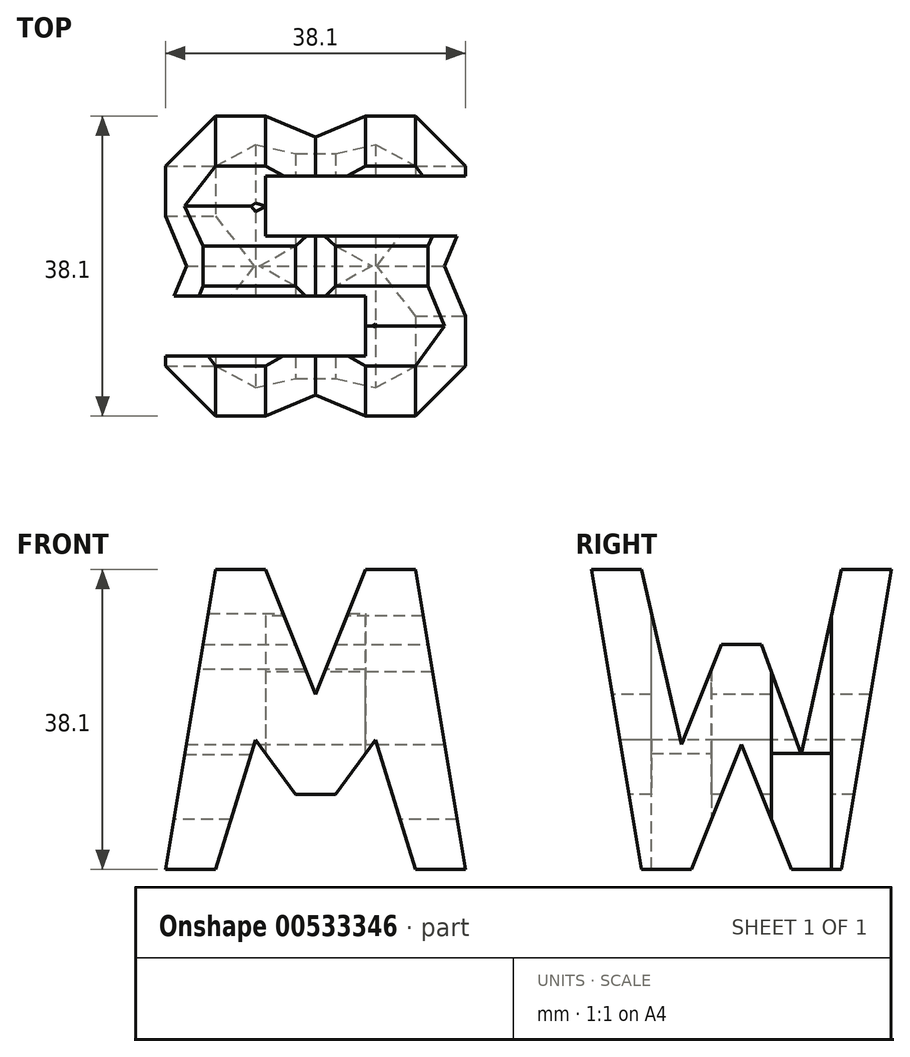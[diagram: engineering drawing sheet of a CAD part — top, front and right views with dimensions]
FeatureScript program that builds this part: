
annotation { "Feature Type Name" : "Feature", "Feature Type Description" : "" }
export const myFeature = defineFeature(function(context is Context, id is Id, definition is map)
    precondition{}
    {
        {
            var Q0;
            Q0=qCreatedBy(makeId("Front.planeOp"),FACE);
            var sketch = newSketch(context, id + "F0", { "sketchPlane" : qUnion([Q0])});
            skLineSegment(sketch, "E0", {"start": v(0, 0) * mm, "end": v(0, 38.1) * mm});
            skLineSegment(sketch, "E1", {"start": v(0, 38.1) * mm, "end": v(38.1, 38.1) * mm});
            skLineSegment(sketch, "E2", {"start": v(38.1, 38.1) * mm, "end": v(38.1, 0) * mm});
            skLineSegment(sketch, "E3", {"start": v(38.1, 0) * mm, "end": v(0, 0) * mm});
            skSolve(sketch);
        }
        {
            var Q0;
            Q0 = qSketchRegion(id + "F0", true);
            extrude(context, id + "F1", {"entities" : qUnion([Q0]), "depth" : 38.1 * mm, "offsetDistance" : 25.4 * mm});
        }
        {
            var Q0;
            Q0=qCreatedBy(makeId("Front.planeOp"),FACE);
            cPlane(context, id + "F2", {"entities" : qUnion([Q0]), "cplaneType" : CPlaneType.OFFSET, "offset" : 38.1 * mm, "width" : 152.4 * mm, "height" : 152.4 * mm});
        }
        {
            var Q0;
            Q0=qCreatedBy(makeId("Right.planeOp"),FACE);
            cPlane(context, id + "F3", {"entities" : qUnion([Q0]), "cplaneType" : CPlaneType.OFFSET, "offset" : 38.1 * mm, "width" : 152.4 * mm, "height" : 152.4 * mm});
        }
        {
            var Q0;
            Q0=qCreatedBy(makeId("Top.planeOp"),FACE);
            cPlane(context, id + "F4", {"entities" : qUnion([Q0]), "cplaneType" : CPlaneType.OFFSET, "offset" : 38.1 * mm, "width" : 152.4 * mm, "height" : 152.4 * mm});
        }
        {
            var Q0;
            Q0=qCreatedBy(id+"F3.planeOp",FACE);
            var sketch = newSketch(context, id + "F5", { "sketchPlane" : qUnion([Q0])});
            skLineSegment(sketch, "E4", {"start": v(0, 0) * mm, "end": v(0, 38.1) * mm});
            skLineSegment(sketch, "E5", {"start": v(0, 38.1) * mm, "end": v(-38.1, 38.1) * mm});
            skLineSegment(sketch, "E6", {"start": v(-38.1, 38.1) * mm, "end": v(-38.1, 0) * mm});
            skLineSegment(sketch, "E7", {"start": v(-38.1, 0) * mm, "end": v(0, 0) * mm});
            skLineSegment(sketch, "E8", {"start": v(-31.75, 38.1) * mm, "end": v(-26.67, 15.88) * mm});
            skLineSegment(sketch, "E9", {"start": v(-26.67, 15.88) * mm, "end": v(-21.59, 28.58) * mm});
            skLineSegment(sketch, "E10", {"start": v(-21.59, 28.58) * mm, "end": v(-16.5, 28.58) * mm});
            skPoint(sketch, "E11.start.orphan", {"position": v(-19.05, 15.88) * mm});
            skPoint(sketch, "E12.end.orphan", {"position": v(-4.03, 38.1) * mm});
            skLineSegment(sketch, "E13", {"start": v(-38.1, 38.1) * mm, "end": v(-31.75, 0) * mm});
            skLineSegment(sketch, "E14", {"start": v(-25.4, 0) * mm, "end": v(-19.05, 15.88) * mm});
            skLineSegment(sketch, "E15", {"start": v(-19.05, 15.88) * mm, "end": v(-12.7, 0) * mm});
            skLineSegment(sketch, "E16", {"start": v(0, 38.1) * mm, "end": v(-6.35, 0) * mm});
            skPoint(sketch, "E17.end.orphan", {"position": v(-6.35, 38.1) * mm});
            skLineSegment(sketch, "E18", {"start": v(-6.35, 38.1) * mm, "end": v(-11.43, 14.59) * mm});
            skPoint(sketch, "E19.end.orphan", {"position": v(-16.7, 15.88) * mm});
            skLineSegment(sketch, "E20", {"start": v(-16.5, 28.58) * mm, "end": v(-11.43, 14.59) * mm});
            skSolve(sketch);
        }
        {
            var Q0;
            {var subQ0=sQuery(id+"F5.wireOp",EDGE,"E8");Q0=makeQuery(id+"F5.imprint","IMPRINT",FACE,{"disambiguationData":[TD([[makeQuery(id+"F5.imprint","IMPRINT",EDGE,{"derivedFrom":subQ0}),1.0]])]});}
            var Q1;
            {var subQ0=sQuery(id+"F5.wireOp",EDGE,"E6");Q1=makeQuery(id+"F5.imprint","IMPRINT",FACE,{"disambiguationData":[TD([[makeQuery(id+"F5.imprint","IMPRINT",EDGE,{"derivedFrom":subQ0}),1.0]])]});}
            var Q2;
            {var subQ0=sQuery(id+"F5.wireOp",EDGE,"E14");Q2=makeQuery(id+"F5.imprint","IMPRINT",FACE,{"disambiguationData":[TD([[makeQuery(id+"F5.imprint","IMPRINT",EDGE,{"derivedFrom":subQ0}),-1.0]])]});}
            var Q3;
            {var subQ0=sQuery(id+"F5.wireOp",EDGE,"E4");Q3=makeQuery(id+"F5.imprint","IMPRINT",FACE,{"disambiguationData":[TD([[makeQuery(id+"F5.imprint","IMPRINT",EDGE,{"derivedFrom":subQ0}),1.0]])]});}
            extrude(context, id + "F6", {"entities" : qUnion([Q0, Q1, Q2, Q3]), "operationType" : NewBodyOperationType.REMOVE, "oppositeDirection" : true, "depth" : 38.1 * mm, "offsetDistance" : 25.4 * mm});
        }
        {
            var Q0;
            Q0=qCreatedBy(id+"F2.planeOp",FACE);
            var sketch = newSketch(context, id + "F7", { "sketchPlane" : qUnion([Q0])});
            skLineSegment(sketch, "E21", {"start": v(0, 0) * mm, "end": v(0, 38.1) * mm});
            skLineSegment(sketch, "E22", {"start": v(0, 38.1) * mm, "end": v(38.1, 38.1) * mm});
            skLineSegment(sketch, "E23", {"start": v(38.1, 38.1) * mm, "end": v(38.1, 0) * mm});
            skLineSegment(sketch, "E24", {"start": v(38.1, 0) * mm, "end": v(0, 0) * mm});
            skLineSegment(sketch, "E25", {"start": v(0, 0) * mm, "end": v(6.35, 38.1) * mm});
            skLineSegment(sketch, "E26", {"start": v(12.7, 38.1) * mm, "end": v(19.05, 22.22) * mm});
            skLineSegment(sketch, "E27", {"start": v(19.05, 22.22) * mm, "end": v(25.4, 38.1) * mm});
            skLineSegment(sketch, "E28", {"start": v(38.1, 0) * mm, "end": v(31.75, 38.1) * mm});
            skLineSegment(sketch, "E29", {"start": v(6.35, 0) * mm, "end": v(11.43, 16.47) * mm});
            skLineSegment(sketch, "E30", {"start": v(11.43, 16.47) * mm, "end": v(16.51, 9.52) * mm});
            skLineSegment(sketch, "E31", {"start": v(16.51, 9.52) * mm, "end": v(21.6, 9.52) * mm});
            skLineSegment(sketch, "E32", {"start": v(21.6, 9.52) * mm, "end": v(26.67, 16.47) * mm});
            skLineSegment(sketch, "E33", {"start": v(26.67, 16.47) * mm, "end": v(31.75, 0) * mm});
            skSolve(sketch);
        }
        {
            var Q0;
            {var subQ0=sQuery(id+"F7.wireOp",EDGE,"E21");Q0=makeQuery(id+"F7.imprint","IMPRINT",FACE,{"disambiguationData":[TD([[makeQuery(id+"F7.imprint","IMPRINT",EDGE,{"derivedFrom":subQ0}),-1.0]])]});}
            var Q1;
            {var subQ0=sQuery(id+"F7.wireOp",EDGE,"E26");Q1=makeQuery(id+"F7.imprint","IMPRINT",FACE,{"disambiguationData":[TD([[makeQuery(id+"F7.imprint","IMPRINT",EDGE,{"derivedFrom":subQ0}),1.0]])]});}
            var Q2;
            {var subQ0=sQuery(id+"F7.wireOp",EDGE,"E29");Q2=makeQuery(id+"F7.imprint","IMPRINT",FACE,{"disambiguationData":[TD([[makeQuery(id+"F7.imprint","IMPRINT",EDGE,{"derivedFrom":subQ0}),-1.0]])]});}
            var Q3;
            {var subQ0=sQuery(id+"F7.wireOp",EDGE,"E23");Q3=makeQuery(id+"F7.imprint","IMPRINT",FACE,{"disambiguationData":[TD([[makeQuery(id+"F7.imprint","IMPRINT",EDGE,{"derivedFrom":subQ0}),-1.0]])]});}
            extrude(context, id + "F8", {"entities" : qUnion([Q0, Q1, Q2, Q3]), "operationType" : NewBodyOperationType.REMOVE, "oppositeDirection" : true, "depth" : 38.1 * mm, "offsetDistance" : 25.4 * mm});
        }
        {
            var Q0;
            Q0=qCreatedBy(id+"F4.planeOp",FACE);
            var sketch = newSketch(context, id + "F9", { "sketchPlane" : qUnion([Q0])});
            skLineSegment(sketch, "E34", {"start": v(0, 0) * mm, "end": v(38.1, 0) * mm});
            skLineSegment(sketch, "E35", {"start": v(38.1, 0) * mm, "end": v(38.1, -38.1) * mm});
            skLineSegment(sketch, "E36", {"start": v(38.1, -38.1) * mm, "end": v(0, -38.1) * mm});
            skLineSegment(sketch, "E37", {"start": v(0, 0) * mm, "end": v(0, -38.1) * mm});
            skLineSegment(sketch, "E38", {"start": v(0, -22.86) * mm, "end": v(25.4, -22.86) * mm});
            skLineSegment(sketch, "E39", {"start": v(25.4, -22.86) * mm, "end": v(25.4, -30.48) * mm});
            skLineSegment(sketch, "E40", {"start": v(25.4, -30.48) * mm, "end": v(0, -30.48) * mm});
            skLineSegment(sketch, "E41", {"start": v(38.1, -7.62) * mm, "end": v(12.7, -7.62) * mm});
            skLineSegment(sketch, "E42", {"start": v(12.7, -7.62) * mm, "end": v(12.7, -15.24) * mm});
            skLineSegment(sketch, "E43", {"start": v(12.7, -15.24) * mm, "end": v(38.1, -15.24) * mm});
            skSolve(sketch);
        }
        {
            var Q0;
            {var subQ0=sQuery(id+"F9.wireOp",EDGE,"E41");Q0=makeQuery(id+"F9.imprint","IMPRINT",FACE,{"disambiguationData":[TD([[makeQuery(id+"F9.imprint","IMPRINT",EDGE,{"derivedFrom":subQ0}),1.0]])]});}
            var Q1;
            {var subQ0=sQuery(id+"F9.wireOp",EDGE,"E38");Q1=makeQuery(id+"F9.imprint","IMPRINT",FACE,{"disambiguationData":[TD([[makeQuery(id+"F9.imprint","IMPRINT",EDGE,{"derivedFrom":subQ0}),-1.0]])]});}
            extrude(context, id + "F10", {"entities" : qUnion([Q0, Q1]), "operationType" : NewBodyOperationType.REMOVE, "oppositeDirection" : true, "depth" : 38.1 * mm, "offsetDistance" : 25.4 * mm});
        }
    });
